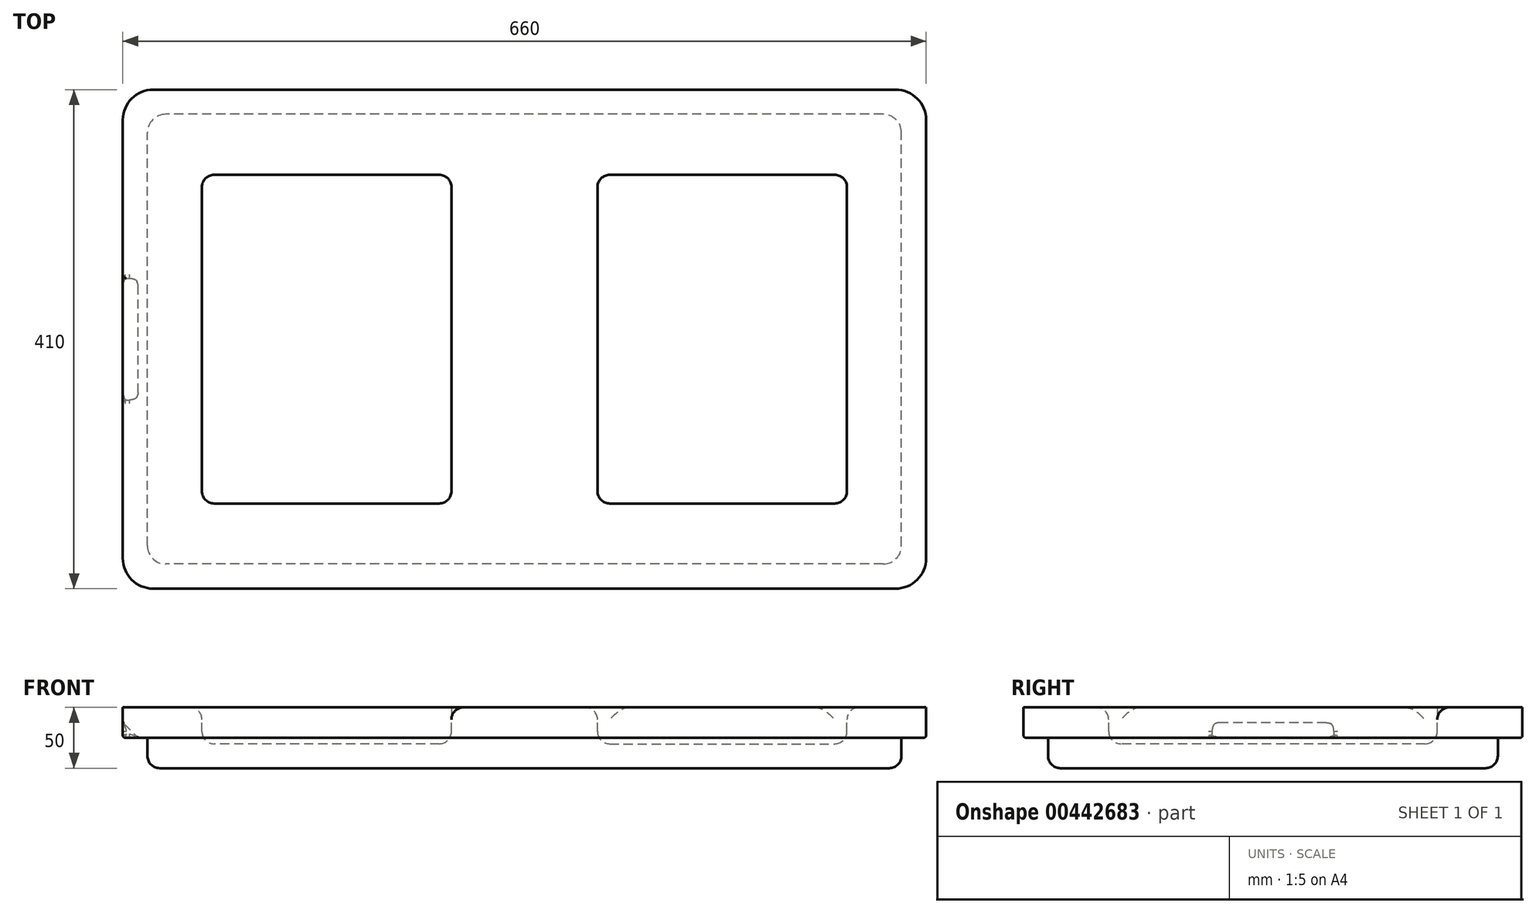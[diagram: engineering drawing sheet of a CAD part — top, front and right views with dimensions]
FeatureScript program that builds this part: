
annotation { "Feature Type Name" : "Feature", "Feature Type Description" : "" }
export const myFeature = defineFeature(function(context is Context, id is Id, definition is map)
    precondition{}
    {
        {
            var Q0;
            Q0=qCreatedBy(makeId("Top.planeOp"),FACE);
            var sketch = newSketch(context, id + "F0", { "sketchPlane" : qUnion([Q0])});
            skLineSegment(sketch, "E0.bottom", {"start": v(330, 205) * mm, "end": v(-330, 205) * mm});
            skLineSegment(sketch, "E0.top", {"start": v(330, -205) * mm, "end": v(-330, -205) * mm});
            skLineSegment(sketch, "E0.left", {"start": v(330, 205) * mm, "end": v(330, -205) * mm});
            skLineSegment(sketch, "E0.right", {"start": v(-330, 205) * mm, "end": v(-330, -205) * mm});
            skPoint(sketch, "E0.middle", {"position": v(0, 0) * mm});
            skSolve(sketch);
        }
        {
            var Q0;
            Q0=makeQuery(id+"F0.imprint","IMPRINT",FACE,{"disambiguationData":[TD([[makeQuery(id+"F0.imprint","IMPRINT",EDGE,{"derivedFrom":sQuery(id+"F0.wireOp",EDGE,"E0.bottom")}),1.0]])]});
            extrude(context, id + "F1", {"entities" : qUnion([Q0]), "oppositeDirection" : true, "depth" : 25 * mm});
        }
        {
            var Q0;
            Q0=makeQuery(id+"F1.opExtrude","CAP_FACE",FACE,{"disambiguationData":[OSD([sQuery(id+"F0.wireOp",EDGE,"E0.bottom"),sQuery(id+"F0.wireOp",EDGE,"E0.top"),sQuery(id+"F0.wireOp",EDGE,"E0.left"),sQuery(id+"F0.wireOp",EDGE,"E0.right")])],"isStart":false});
            var sketch = newSketch(context, id + "F2", { "sketchPlane" : qUnion([Q0])});
            skLineSegment(sketch, "E1.bottom", {"start": v(309.75, 184.75) * mm, "end": v(-309.75, 184.75) * mm});
            skLineSegment(sketch, "E1.top", {"start": v(309.75, -184.75) * mm, "end": v(-309.75, -184.75) * mm});
            skLineSegment(sketch, "E1.left", {"start": v(309.75, 184.75) * mm, "end": v(309.75, -184.75) * mm});
            skLineSegment(sketch, "E1.right", {"start": v(-309.75, 184.75) * mm, "end": v(-309.75, -184.75) * mm});
            skPoint(sketch, "E1.middle", {"position": v(0, 0) * mm});
            skSolve(sketch);
        }
        {
            var Q0;
            Q0=makeQuery(id+"F2.imprint","IMPRINT",FACE,{"disambiguationData":[TD([[makeQuery(id+"F2.imprint","IMPRINT",EDGE,{"derivedFrom":sQuery(id+"F2.wireOp",EDGE,"E1.bottom")}),1.0]])]});
            extrude(context, id + "F3", {"entities" : qUnion([Q0]), "operationType" : NewBodyOperationType.ADD, "depth" : 25 * mm});
        }
        {
            var Q0;
            Q0=makeQuery(id+"F1.opExtrude","CAP_FACE",FACE,{"disambiguationData":[OSD([sQuery(id+"F0.wireOp",EDGE,"E0.bottom"),sQuery(id+"F0.wireOp",EDGE,"E0.top"),sQuery(id+"F0.wireOp",EDGE,"E0.left"),sQuery(id+"F0.wireOp",EDGE,"E0.right")])],"isStart":true});
            var sketch = newSketch(context, id + "F4", { "sketchPlane" : qUnion([Q0])});
            skLineSegment(sketch, "E2", {"start": v(-437.6, 0) * mm, "end": v(442.87, 0) * mm, "construction": true});
            skPoint(sketch, "E2.endSnap0", {"position": v(-330, 0) * mm});
            skLineSegment(sketch, "E3.bottom", {"start": v(-60, 135) * mm, "end": v(-265, 135) * mm});
            skLineSegment(sketch, "E3.top", {"start": v(-60, -135) * mm, "end": v(-265, -135) * mm});
            skLineSegment(sketch, "E3.left", {"start": v(-60, 135) * mm, "end": v(-60, -135) * mm});
            skLineSegment(sketch, "E3.right", {"start": v(-265, 135) * mm, "end": v(-265, -135) * mm});
            skPoint(sketch, "E3.middle", {"position": v(-162.5, 0) * mm});
            skLineSegment(sketch, "E4", {"start": v(0, 232.06) * mm, "end": v(0, -242.3) * mm, "construction": true});
            skPoint(sketch, "E4.endSnap0", {"position": v(0, -205) * mm});
            skLineSegment(sketch, "E5.MirrorCS", {"start": v(60, 135) * mm, "end": v(60, -135) * mm});
            skLineSegment(sketch, "E6.MirrorCS", {"start": v(60, 135) * mm, "end": v(265, 135) * mm});
            skLineSegment(sketch, "E7.MirrorCS", {"start": v(265, 135) * mm, "end": v(265, -135) * mm});
            skLineSegment(sketch, "E8.MirrorCS", {"start": v(60, -135) * mm, "end": v(265, -135) * mm});
            skSolve(sketch);
        }
        {
            var Q0;
            Q0=makeQuery(id+"F4.imprint","IMPRINT",FACE,{"disambiguationData":[TD([[makeQuery(id+"F4.imprint","IMPRINT",EDGE,{"derivedFrom":sQuery(id+"F4.wireOp",EDGE,"E3.bottom")}),1.0]])]});
            var Q1;
            Q1=makeQuery(id+"F4.imprint","IMPRINT",FACE,{"disambiguationData":[TD([[makeQuery(id+"F4.imprint","IMPRINT",EDGE,{"derivedFrom":sQuery(id+"F4.wireOp",EDGE,"E5.MirrorCS")}),1.0]])]});
            extrude(context, id + "F5", {"entities" : qUnion([Q0, Q1]), "operationType" : NewBodyOperationType.REMOVE, "oppositeDirection" : true, "depth" : 30 * mm});
        }
        {
            var Q0;
            Q0=makeQuery(id+"F1.opExtrude","SWEPT_FACE",FACE,{"disambiguationData":[OSD([sQuery(id+"F0.wireOp",EDGE,"E0.right")])]});
            var sketch = newSketch(context, id + "F6", { "sketchPlane" : qUnion([Q0])});
            skLineSegment(sketch, "E9.bottom", {"start": v(-50, -25) * mm, "end": v(50, -25) * mm});
            skLineSegment(sketch, "E9.top", {"start": v(-50, -12.5) * mm, "end": v(50, -12.5) * mm});
            skLineSegment(sketch, "E9.left", {"start": v(-50, -25) * mm, "end": v(-50, -12.5) * mm});
            skLineSegment(sketch, "E9.right", {"start": v(50, -25) * mm, "end": v(50, -12.5) * mm});
            skLineSegment(sketch, "E10", {"start": v(0, 79.77) * mm, "end": v(0, -93.63) * mm, "construction": true});
            skSolve(sketch);
        }
        {
            var Q0;
            Q0=qCreatedBy(makeId("Front.planeOp"),FACE);
            var sketch = newSketch(context, id + "F7", { "sketchPlane" : qUnion([Q0])});
            skLineSegment(sketch, "E11", {"start": v(-330, -12.5) * mm, "end": v(-314.44, -28.06) * mm});
            skSolve(sketch);
        }
        {
            var Q0;
            Q0=makeQuery(id+"F6.imprint","IMPRINT",FACE,{"disambiguationData":[TD([[makeQuery(id+"F6.imprint","IMPRINT",EDGE,{"derivedFrom":sQuery(id+"F6.wireOp",EDGE,"E9.bottom")}),1.0]])]});
            var Q1;
            Q1=sQuery(id+"F7.wireOp",EDGE,"E11");
            sweep(context, id + "F8", {"operationType" : NewBodyOperationType.REMOVE, "profiles" : qUnion([Q0]), "path" : qUnion([Q1])});
        }
        {
            var Q0;
            Q0=makeQuery(id+"F1.opExtrude","SWEPT_EDGE",EDGE,{"disambiguationData":[OSD([sQuery(id+"F0.wireOp",EDGE,"E0.bottom"),sQuery(id+"F0.wireOp",EDGE,"E0.right")])]});
            var Q1;
            Q1=makeQuery(id+"F1.opExtrude","SWEPT_EDGE",EDGE,{"disambiguationData":[OSD([sQuery(id+"F0.wireOp",EDGE,"E0.top"),sQuery(id+"F0.wireOp",EDGE,"E0.right")])]});
            var Q2;
            Q2=makeQuery(id+"F1.opExtrude","SWEPT_EDGE",EDGE,{"disambiguationData":[OSD([sQuery(id+"F0.wireOp",EDGE,"E0.top"),sQuery(id+"F0.wireOp",EDGE,"E0.left")])]});
            var Q3;
            Q3=makeQuery(id+"F1.opExtrude","SWEPT_EDGE",EDGE,{"disambiguationData":[OSD([sQuery(id+"F0.wireOp",EDGE,"E0.bottom"),sQuery(id+"F0.wireOp",EDGE,"E0.left")])]});
            fillet(context, id + "F9", {"entities" : qUnion([Q0, Q1, Q2, Q3]), "radius" : 25 * mm, "tangentPropagation" : true, "allowEdgeOverflow" : false});
        }
        {
            var Q0;
            Q0=makeQuery(id+"F3.opExtrude","SWEPT_EDGE",EDGE,{"disambiguationData":[OSD([sQuery(id+"F2.wireOp",EDGE,"E1.top"),sQuery(id+"F2.wireOp",EDGE,"E1.right")])]});
            var Q1;
            Q1=makeQuery(id+"F3.opExtrude","SWEPT_EDGE",EDGE,{"disambiguationData":[OSD([sQuery(id+"F2.wireOp",EDGE,"E1.bottom"),sQuery(id+"F2.wireOp",EDGE,"E1.right")])]});
            var Q2;
            Q2=makeQuery(id+"F3.opExtrude","SWEPT_EDGE",EDGE,{"disambiguationData":[OSD([sQuery(id+"F2.wireOp",EDGE,"E1.bottom"),sQuery(id+"F2.wireOp",EDGE,"E1.left")])]});
            var Q3;
            Q3=makeQuery(id+"F3.opExtrude","SWEPT_EDGE",EDGE,{"disambiguationData":[OSD([sQuery(id+"F2.wireOp",EDGE,"E1.top"),sQuery(id+"F2.wireOp",EDGE,"E1.left")])]});
            fillet(context, id + "F10", {"entities" : qUnion([Q0, Q1, Q2, Q3]), "radius" : 15 * mm, "tangentPropagation" : true, "allowEdgeOverflow" : false});
        }
        {
            var Q0;
            Q0=makeQuery(id+"F5.boolean.opBoolean","COPY",FACE,{"derivedFrom":makeQuery(id+"F5.opExtrude","CAP_FACE",FACE,{"disambiguationData":[OSD([sQuery(id+"F4.wireOp",EDGE,"E3.bottom"),sQuery(id+"F4.wireOp",EDGE,"E3.top"),sQuery(id+"F4.wireOp",EDGE,"E3.left"),sQuery(id+"F4.wireOp",EDGE,"E3.right")])],"isStart":false})});
            var Q1;
            Q1=makeQuery(id+"F5.boolean.opBoolean","COPY",FACE,{"derivedFrom":makeQuery(id+"F5.opExtrude","CAP_FACE",FACE,{"disambiguationData":[OSD([sQuery(id+"F4.wireOp",EDGE,"E5.MirrorCS"),sQuery(id+"F4.wireOp",EDGE,"E6.MirrorCS"),sQuery(id+"F4.wireOp",EDGE,"E7.MirrorCS"),sQuery(id+"F4.wireOp",EDGE,"E8.MirrorCS")])],"isStart":false})});
            var Q2;
            Q2=makeQuery(id+"F5.boolean.opBoolean","COPY",FACE,{"derivedFrom":makeQuery(id+"F5.opExtrude","SWEPT_FACE",FACE,{"disambiguationData":[OSD([sQuery(id+"F4.wireOp",EDGE,"E3.bottom")])]})});
            var Q3;
            Q3=makeQuery(id+"F5.boolean.opBoolean","COPY",FACE,{"derivedFrom":makeQuery(id+"F5.opExtrude","SWEPT_FACE",FACE,{"disambiguationData":[OSD([sQuery(id+"F4.wireOp",EDGE,"E3.right")])]})});
            var Q4;
            Q4=makeQuery(id+"F5.boolean.opBoolean","COPY",FACE,{"derivedFrom":makeQuery(id+"F5.opExtrude","SWEPT_FACE",FACE,{"disambiguationData":[OSD([sQuery(id+"F4.wireOp",EDGE,"E3.top")])]})});
            var Q5;
            Q5=makeQuery(id+"F5.boolean.opBoolean","COPY",EDGE,{"derivedFrom":makeQuery(id+"F5.opExtrude","CAP_EDGE",EDGE,{"disambiguationData":[OSD([sQuery(id+"F4.wireOp",EDGE,"E6.MirrorCS")])],"isStart":false})});
            var Q6;
            Q6=makeQuery(id+"F5.boolean.opBoolean","COPY",FACE,{"derivedFrom":makeQuery(id+"F5.opExtrude","SWEPT_FACE",FACE,{"disambiguationData":[OSD([sQuery(id+"F4.wireOp",EDGE,"E7.MirrorCS")])]})});
            var Q7;
            Q7=makeQuery(id+"F5.boolean.opBoolean","COPY",FACE,{"derivedFrom":makeQuery(id+"F5.opExtrude","SWEPT_FACE",FACE,{"disambiguationData":[OSD([sQuery(id+"F4.wireOp",EDGE,"E8.MirrorCS")])]})});
            var Q8;
            Q8=makeQuery(id+"F5.boolean.opBoolean","COPY",FACE,{"derivedFrom":makeQuery(id+"F5.opExtrude","SWEPT_FACE",FACE,{"disambiguationData":[OSD([sQuery(id+"F4.wireOp",EDGE,"E5.MirrorCS")])]})});
            var Q9;
            Q9=makeQuery(id+"F3.opExtrude","CAP_FACE",FACE,{"disambiguationData":[OSD([sQuery(id+"F2.wireOp",EDGE,"E1.bottom"),sQuery(id+"F2.wireOp",EDGE,"E1.top"),sQuery(id+"F2.wireOp",EDGE,"E1.left"),sQuery(id+"F2.wireOp",EDGE,"E1.right")])],"isStart":false});
            fillet(context, id + "F11", {"entities" : qUnion([Q0, Q1, Q2, Q3, Q4, Q5, Q6, Q7, Q8, Q9]), "radius" : 10 * mm, "tangentPropagation" : true, "allowEdgeOverflow" : false});
        }
        {
            var Q0;
            Q0=makeQuery(id+"F1.opExtrude","CAP_EDGE",EDGE,{"disambiguationData":[OSD([sQuery(id+"F0.wireOp",EDGE,"E0.top")])],"isStart":false});
            var Q1;
            {var subQ0=sQuery(id+"F0.wireOp",EDGE,"E0.bottom");var subQ1=sQuery(id+"F0.wireOp",EDGE,"E0.left");Q1=makeQuery(id+"FmmFjA9vbV3kZRA_1.1.F8.boolean.opBoolean","SPLIT",EDGE,{"disambiguationData":[TD([makeQuery(id+"F1.opExtrude","SWEPT_FACE",FACE,{"disambiguationData":[OSD([subQ0])]})])],"derivedFrom":makeQuery(id+"F1.opExtrude","CAP_EDGE",EDGE,{"disambiguationData":[OSD([subQ1])],"isStart":false})});}
            fillet(context, id + "F12", {"entities" : qUnion([Q0, Q1]), "radius" : 2 * mm, "tangentPropagation" : true, "allowEdgeOverflow" : false});
        }
        {
            var Q0;
            Q0=makeQuery(id+"F8.boolean.opBoolean","COPY",FACE,{"derivedFrom":makeQuery(id+"F8.opSweep","SWEPT_FACE",FACE,{"disambiguationData":[OSD([sQuery(id+"F6.wireOp",EDGE,"E9.left"),sQuery(id+"F7.wireOp",EDGE,"E11")])]})});
            var Q1;
            Q1=makeQuery(id+"F8.boolean.opBoolean","COPY",FACE,{"derivedFrom":makeQuery(id+"F8.opSweep","SWEPT_FACE",FACE,{"disambiguationData":[OSD([sQuery(id+"F6.wireOp",EDGE,"E9.right"),sQuery(id+"F7.wireOp",EDGE,"E11")])]})});
            var Q2;
            Q2=makeQuery(id+"FmmFjA9vbV3kZRA_1.1.F8.boolean.opBoolean","COPY",FACE,{"derivedFrom":makeQuery(id+"FmmFjA9vbV3kZRA_1.1.F8.opSweep","SWEPT_FACE",FACE,{"disambiguationData":[OSD([sQuery(id+"F6.wireOp",EDGE,"E9.right"),sQuery(id+"F7.wireOp",EDGE,"E11")])]})});
            var Q3;
            Q3=makeQuery(id+"FmmFjA9vbV3kZRA_1.1.F8.boolean.opBoolean","COPY",FACE,{"derivedFrom":makeQuery(id+"FmmFjA9vbV3kZRA_1.1.F8.opSweep","SWEPT_FACE",FACE,{"disambiguationData":[OSD([sQuery(id+"F6.wireOp",EDGE,"E9.left"),sQuery(id+"F7.wireOp",EDGE,"E11")])]})});
            fillet(context, id + "F13", {"entities" : qUnion([Q0, Q1, Q2, Q3]), "radius" : 3 * mm, "tangentPropagation" : true, "allowEdgeOverflow" : false});
        }
    });
